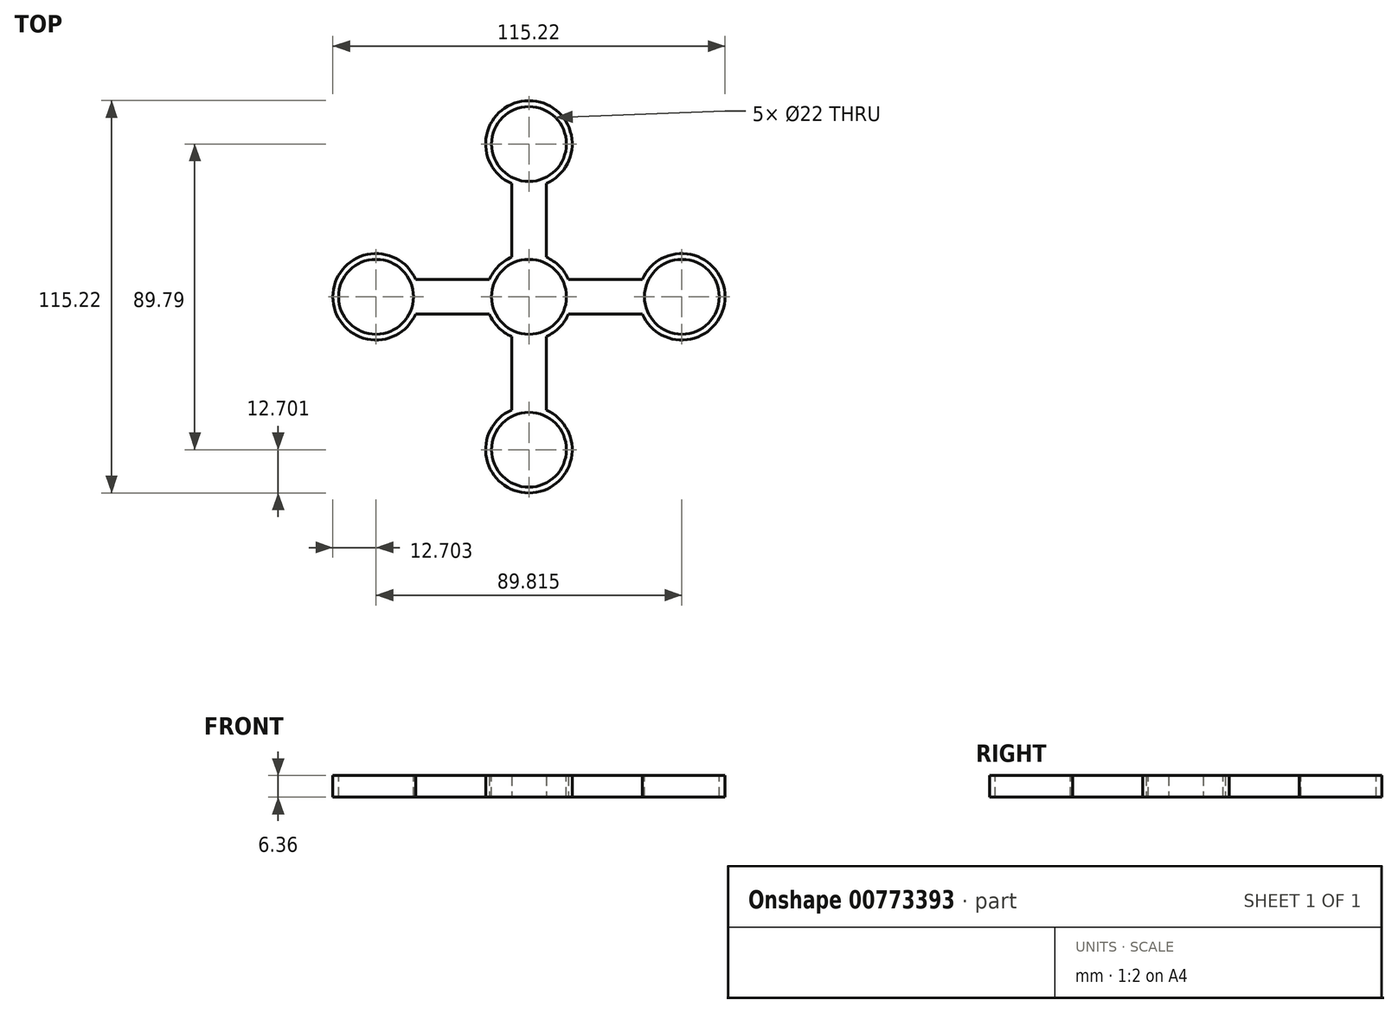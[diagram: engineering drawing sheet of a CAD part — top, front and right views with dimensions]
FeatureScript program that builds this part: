
annotation { "Feature Type Name" : "Feature", "Feature Type Description" : "" }
export const myFeature = defineFeature(function(context is Context, id is Id, definition is map)
    precondition{}
    {
        {
            var Q0;
            Q0=qCreatedBy(makeId("Top.planeOp"),FACE);
            var sketch = newSketch(context, id + "F0", { "sketchPlane" : qUnion([Q0])});
            skLineSegment(sketch, "E0.bottom", {"start": v(-5.08, 9.76) * mm, "end": v(5.08, 9.76) * mm});
            skLineSegment(sketch, "E0.top", {"start": v(-5.08, 35.16) * mm, "end": v(5.08, 35.16) * mm});
            skLineSegment(sketch, "E0.left", {"start": v(-5.08, 9.76) * mm, "end": v(-5.08, 35.16) * mm});
            skLineSegment(sketch, "E0.right", {"start": v(5.08, 9.76) * mm, "end": v(5.08, 35.16) * mm});
            skPoint(sketch, "E0.middle", {"position": v(0, 22.46) * mm});
            skLineSegment(sketch, "E1.bottom", {"start": v(-5.08, -35.15) * mm, "end": v(5.08, -35.15) * mm});
            skLineSegment(sketch, "E1.top", {"start": v(-5.08, -9.75) * mm, "end": v(5.08, -9.75) * mm});
            skLineSegment(sketch, "E1.left", {"start": v(-5.08, -35.15) * mm, "end": v(-5.08, -9.75) * mm});
            skLineSegment(sketch, "E1.right", {"start": v(5.08, -35.15) * mm, "end": v(5.08, -9.75) * mm});
            skPoint(sketch, "E1.middle", {"position": v(0, -22.45) * mm});
            skLineSegment(sketch, "E2.bottom", {"start": v(-9.75, -5.08) * mm, "end": v(-35.15, -5.08) * mm});
            skLineSegment(sketch, "E2.top", {"start": v(-9.75, 5.08) * mm, "end": v(-35.15, 5.08) * mm});
            skLineSegment(sketch, "E2.left", {"start": v(-9.75, -5.08) * mm, "end": v(-9.75, 5.08) * mm});
            skLineSegment(sketch, "E2.right", {"start": v(-35.15, -5.08) * mm, "end": v(-35.15, 5.08) * mm});
            skPoint(sketch, "E2.middle", {"position": v(-22.45, 0) * mm});
            skLineSegment(sketch, "E3.bottom", {"start": v(35.15, -5.08) * mm, "end": v(9.75, -5.08) * mm});
            skLineSegment(sketch, "E3.top", {"start": v(35.15, 5.08) * mm, "end": v(9.75, 5.08) * mm});
            skLineSegment(sketch, "E3.left", {"start": v(35.15, -5.08) * mm, "end": v(35.15, 5.08) * mm});
            skLineSegment(sketch, "E3.right", {"start": v(9.75, -5.08) * mm, "end": v(9.75, 5.08) * mm});
            skPoint(sketch, "E3.middle", {"position": v(22.45, 0) * mm});
            skCircle(sketch, "E4", {"center": v(0, 0) * mm, "radius": 12.7 * mm});
            skCircle(sketch, "E5", {"center": v(44.9, 0) * mm, "radius": 12.7 * mm});
            skCircle(sketch, "E6", {"center": v(0, -44.9) * mm, "radius": 12.7 * mm});
            skCircle(sketch, "E7", {"center": v(0, 44.9) * mm, "radius": 12.7 * mm});
            skCircle(sketch, "E8", {"center": v(-44.9, 0) * mm, "radius": 12.7 * mm});
            skSolve(sketch);
        }
        {
            var Q0;
            Q0=qCreatedBy(makeId("Top.planeOp"),FACE);
            var sketch = newSketch(context, id + "F1", { "sketchPlane" : qUnion([Q0])});
            skCircle(sketch, "E9", {"center": v(0, 44.88) * mm, "radius": 11 * mm});
            skCircle(sketch, "E10", {"center": v(44.9, 0) * mm, "radius": 11 * mm});
            skCircle(sketch, "E11", {"center": v(-44.9, 0) * mm, "radius": 11 * mm});
            skCircle(sketch, "E12", {"center": v(0, -44.9) * mm, "radius": 11 * mm});
            skCircle(sketch, "E13", {"center": v(0, 0) * mm, "radius": 11 * mm});
            skSolve(sketch);
        }
        {
            var Q0;
            Q0 = qSketchRegion(id + "F0", true);
            extrude(context, id + "F2", {"entities" : qUnion([Q0]), "endBound" : BoundingType.SYMMETRIC, "depth" : 6.35 * mm, "offsetDistance" : 25.4 * mm});
        }
        {
            var Q0;
            Q0 = qSketchRegion(id + "F1", true);
            extrude(context, id + "F3", {"entities" : qUnion([Q0]), "operationType" : NewBodyOperationType.REMOVE, "endBound" : BoundingType.SYMMETRIC, "oppositeDirection" : true, "depth" : 6.35 * mm, "offsetDistance" : 25.4 * mm});
        }
    });
